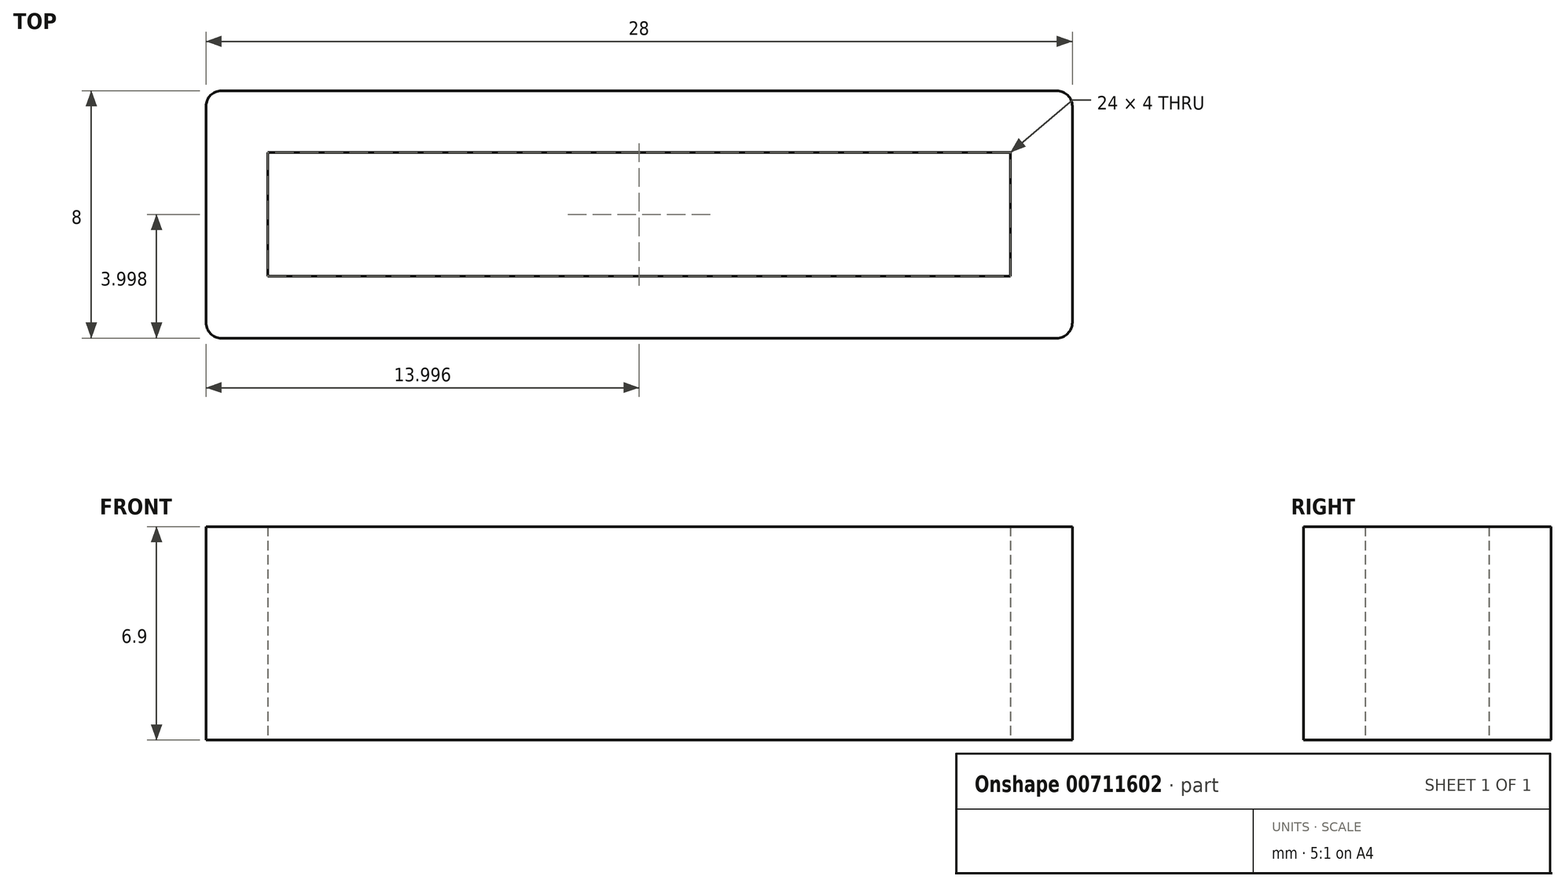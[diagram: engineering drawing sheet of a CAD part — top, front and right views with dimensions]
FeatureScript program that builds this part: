
annotation { "Feature Type Name" : "Feature", "Feature Type Description" : "" }
export const myFeature = defineFeature(function(context is Context, id is Id, definition is map)
    precondition{}
    {
        {
            var Q0;
            Q0=qCreatedBy(makeId("Top.planeOp"),FACE);
            var sketch = newSketch(context, id + "F0", { "sketchPlane" : qUnion([Q0])});
            skLineSegment(sketch, "E0.bottom", {"start": v(-8.54, -1.9) * mm, "end": v(15.46, -1.9) * mm});
            skLineSegment(sketch, "E0.top", {"start": v(-8.54, -5.9) * mm, "end": v(15.46, -5.9) * mm});
            skLineSegment(sketch, "E0.left", {"start": v(-8.54, -1.9) * mm, "end": v(-8.54, -5.9) * mm});
            skLineSegment(sketch, "E0.right", {"start": v(15.46, -1.9) * mm, "end": v(15.46, -5.9) * mm});
            skLineSegment(sketch, "E1.0", {"start": v(-10.04, 0.1) * mm, "end": v(16.96, 0.1) * mm});
            skLineSegment(sketch, "E1.1", {"start": v(-10.54, -0.4) * mm, "end": v(-10.54, -7.4) * mm});
            skLineSegment(sketch, "E1.2", {"start": v(-10.04, -7.9) * mm, "end": v(16.96, -7.9) * mm});
            skLineSegment(sketch, "E1.3", {"start": v(17.46, -0.4) * mm, "end": v(17.46, -7.4) * mm});
            skPoint(sketch, "E2.visualSharp", {"position": v(-10.54, -7.9) * mm});
            skArc(sketch, "E2.filletArc", {"start": v(-10.54, -7.4) * mm, "mid": v(-10.4, -7.75) * mm, "end": v(-10.04, -7.9) * mm});
            skPoint(sketch, "E3.visualSharp", {"position": v(-10.54, 0.1) * mm});
            skArc(sketch, "E3.filletArc", {"start": v(-10.04, 0.1) * mm, "mid": v(-10.4, -0.04) * mm, "end": v(-10.54, -0.4) * mm});
            skPoint(sketch, "E4.visualSharp", {"position": v(17.46, 0.1) * mm});
            skArc(sketch, "E4.filletArc", {"start": v(17.46, -0.4) * mm, "mid": v(17.3, -0.04) * mm, "end": v(16.96, 0.1) * mm});
            skPoint(sketch, "E5.visualSharp", {"position": v(17.46, -7.9) * mm});
            skArc(sketch, "E5.filletArc", {"start": v(16.96, -7.9) * mm, "mid": v(17.3, -7.75) * mm, "end": v(17.46, -7.4) * mm});
            skSolve(sketch);
        }
        {
            var Q0;
            Q0=makeQuery(id+"F0.imprint","IMPRINT",FACE,{"disambiguationData":[TD([[makeQuery(id+"F0.imprint","IMPRINT",EDGE,{"derivedFrom":sQuery(id+"F0.wireOp",EDGE,"E0.bottom")}),1.0]])]});
            extrude(context, id + "F1", {"entities" : qUnion([Q0]), "depth" : 6.9 * mm, "offsetDistance" : 25 * mm});
        }
    });
